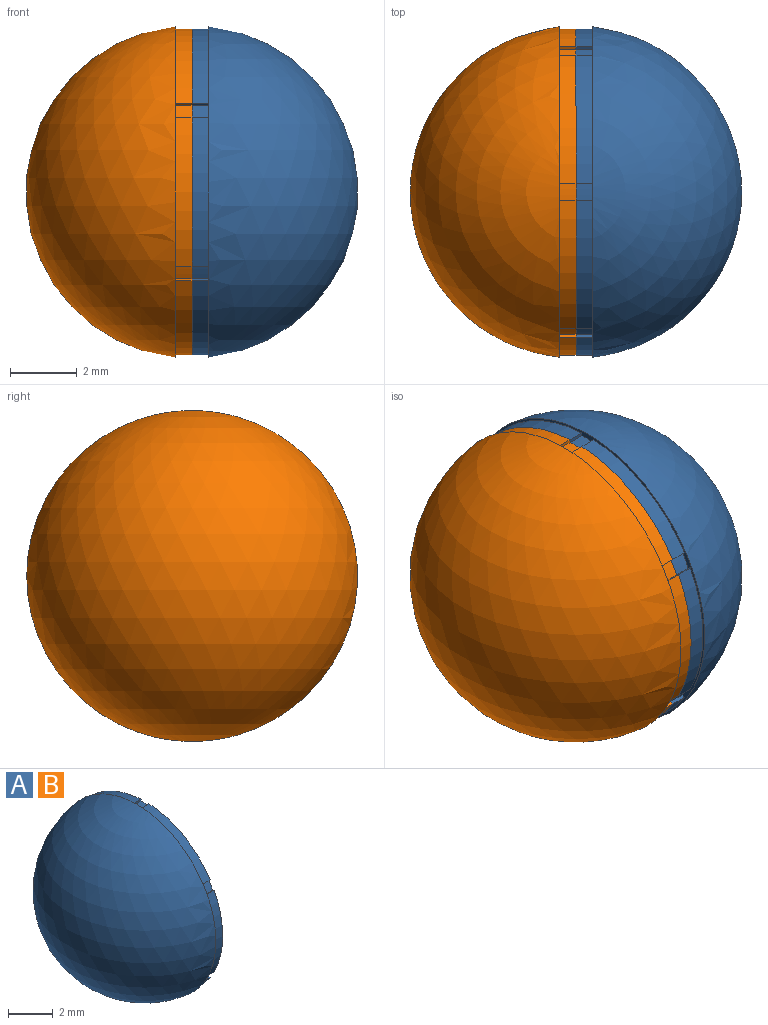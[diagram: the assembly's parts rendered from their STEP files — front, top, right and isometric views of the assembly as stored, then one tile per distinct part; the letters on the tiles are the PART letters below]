
ASSEMBLY  parts=2 mates=1
PART A: 28 faces, bbox 5x10x10 mm
  f0: plane 9.8x9.79mm, normal (1,0,0), area 5.7mm2, adj f1,f2,f3,f4,f5,f6,f7,f8
  f1: sphere r=4.7mm, area 138.8mm2, adj f0
  f2: cylinder r=4.9mm len=3.86mm, axis (1,0,0), area 2.3mm2, adj f0,f3,f25,f26
  f3: plane 0.5x0.1mm, normal (0,1,0), area 0.1mm2, adj f0,f2,f4,f26
  f4: cylinder r=4.8mm len=0.5mm, axis (1,0,0), area 0.3mm2, adj f0,f3,f5,f26
  f5: plane 0.5x0.1mm, normal (0,-1,0), area 0.1mm2, adj f0,f4,f6,f26
  f6: cylinder r=4.9mm len=3.86mm, axis (1,0,0), area 2.3mm2, adj f0,f5,f7,f26
  f7: plane 0.5x0.09mm, normal (0,0.5,-0.87), area 0.1mm2, adj f0,f6,f8,f26
  f8: cylinder r=4.8mm len=0.5mm, axis (1,0,0), area 0.3mm2, adj f0,f7,f9,f26
  f9: plane 0.5x0.09mm, normal (0,-0.5,0.87), area 0.1mm2, adj f0,f8,f10,f26
  f10: cylinder r=4.9mm len=4.46mm, axis (1,0,0), area 2.3mm2, adj f0,f9,f11,f26
  f11: plane 0.5x0.09mm, normal (0,-0.5,-0.87), area 0.1mm2, adj f0,f10,f12,f26
  f12: cylinder r=4.8mm len=0.5mm, axis (1,0,0), area 0.3mm2, adj f0,f11,f13,f26
  f13: plane 0.5x0.09mm, normal (0,0.5,0.87), area 0.1mm2, adj f0,f12,f14,f26
  f14: cylinder r=4.9mm len=3.86mm, axis (1,0,0), area 2.3mm2, adj f0,f13,f15,f26
  f15: plane 0.5x0.1mm, normal (0,-1,0), area 0.1mm2, adj f0,f14,f16,f26
  f16: cylinder r=4.8mm len=0.5mm, axis (1,0,0), area 0.3mm2, adj f0,f15,f17,f26
  f17: plane 0.5x0.1mm, normal (0,1,0), area 0.1mm2, adj f0,f16,f18,f26
  f18: cylinder r=4.9mm len=3.86mm, axis (1,0,0), area 2.3mm2, adj f0,f17,f19,f26
  f19: plane 0.5x0.09mm, normal (0,-0.5,0.87), area 0.1mm2, adj f0,f18,f20,f26
  f20: cylinder r=4.8mm len=0.5mm, axis (1,0,0), area 0.3mm2, adj f0,f19,f21,f26
  f21: plane 0.5x0.09mm, normal (0,0.5,-0.87), area 0.1mm2, adj f0,f20,f22,f26
  f22: cylinder r=4.9mm len=4.46mm, axis (1,0,0), area 2.3mm2, adj f0,f21,f23,f26
  f23: plane 0.5x0.09mm, normal (0,0.5,0.87), area 0.1mm2, adj f0,f22,f24,f26
  f24: cylinder r=4.8mm len=0.5mm, axis (1,0,0), area 0.3mm2, adj f0,f23,f25,f26
  f25: plane 0.5x0.09mm, normal (0,-0.5,-0.87), area 0.1mm2, adj f0,f2,f24,f26
  f26: plane 9.95x9.95mm, normal (1,0,0), area 2.6mm2, adj f2,f3,f4,f5,f6,f7,f8,f9
  f27: sphere r=5mm, area 141.4mm2, adj f26
PART B: same geometry as A
PLACE A rot(axis=(0,-1,0),180deg) t=(-15.92,-9.55,-0.55)mm
PLACE B t=(-15.92,-9.55,-0.55)mm
MATE cylindrical A.f20 <-> B.f20  axis (-1,0,0) through (-15.92,-9.55,-0.55)mm
